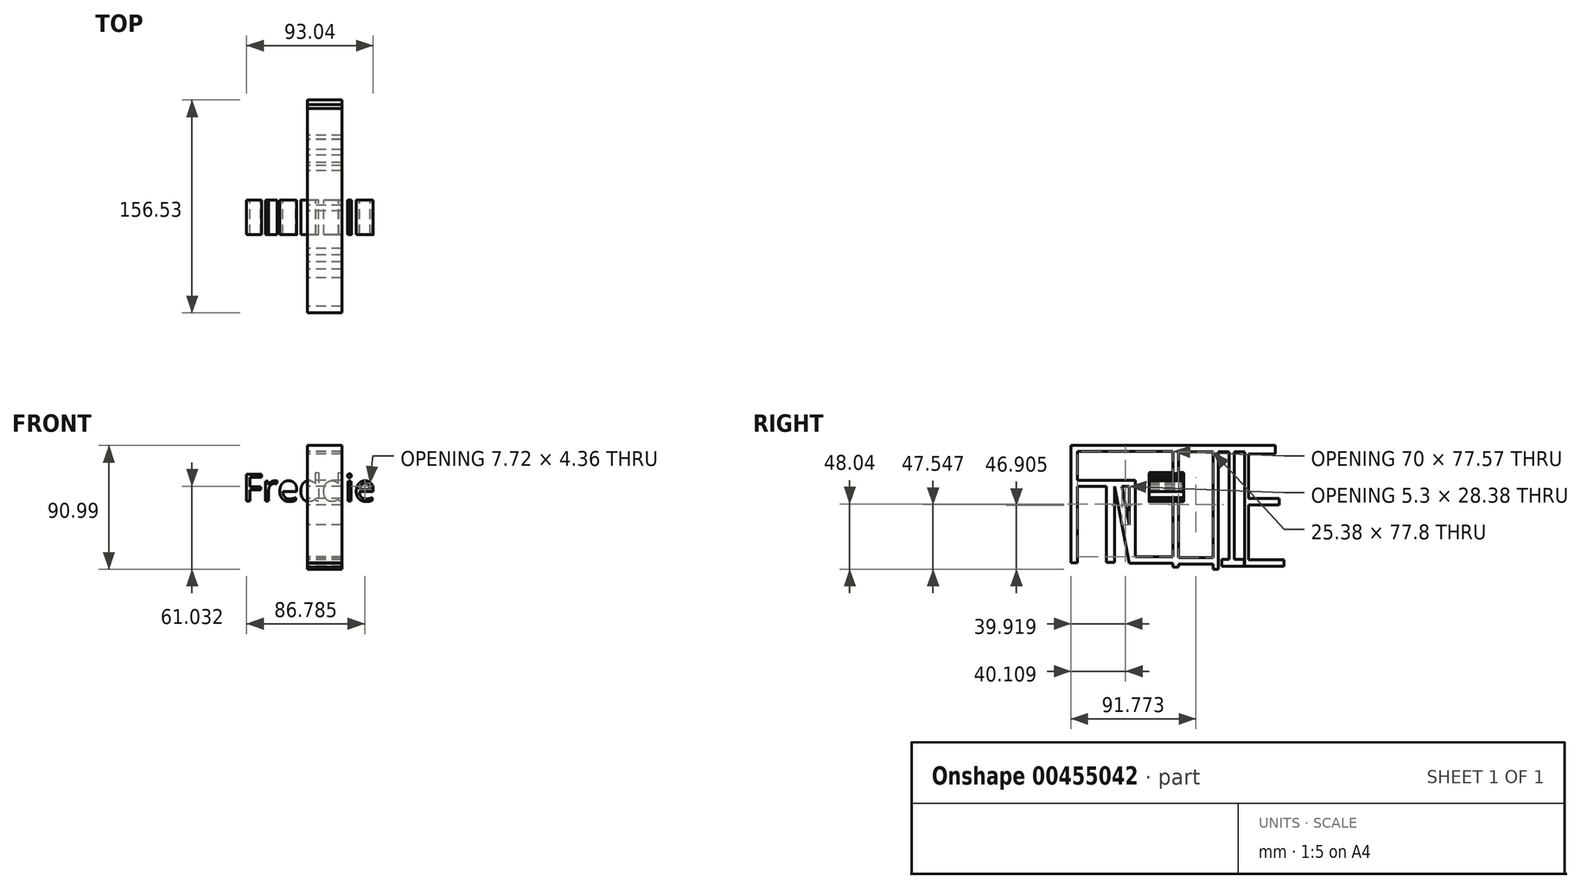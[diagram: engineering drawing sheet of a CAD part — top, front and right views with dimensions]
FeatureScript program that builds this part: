
annotation { "Feature Type Name" : "Feature", "Feature Type Description" : "" }
export const myFeature = defineFeature(function(context is Context, id is Id, definition is map)
    precondition{}
    {
        {
            var Q0;
            Q0=qCreatedBy(makeId("Front.planeOp"),FACE);
            var sketch = newSketch(context, id + "F0", { "sketchPlane" : qUnion([Q0])});
            skText(sketch, "E0", { "text": " Freddie\n", "fontName": "OpenSans-Regular.ttf"});
            const initialGuessF0  = {"E0": [-0.05437, 0, 1, 0, 0.01985]};
            skSetInitialGuess(sketch, initialGuessF0);
            skSolve(sketch);
        }
        {
            var Q0;
            Q0 = qSketchRegion(id + "F0", true);
            var Q1;
            Q1=makeQuery(id+"F0.imprint","IMPRINT",FACE,{"disambiguationData":[TD([[makeQuery(id+"F0.imprint","IMPRINT",EDGE,{"derivedFrom":sQuery(id+"F0.wireOp",EDGE,"E0.sketch_text.stroke-102")}),-1.0]])]});
            var Q2;
            Q2=makeQuery(id+"F0.imprint","IMPRINT",FACE,{"disambiguationData":[TD([[makeQuery(id+"F0.imprint","IMPRINT",EDGE,{"derivedFrom":sQuery(id+"F0.wireOp",EDGE,"E0.sketch_text.stroke-66")}),-1.0]])]});
            var Q3;
            Q3=makeQuery(id+"F0.imprint","IMPRINT",FACE,{"disambiguationData":[TD([[makeQuery(id+"F0.imprint","IMPRINT",EDGE,{"derivedFrom":sQuery(id+"F0.wireOp",EDGE,"E0.sketch_text.stroke-81")}),1.0]])]});
            var Q4;
            Q4=makeQuery(id+"F0.imprint","IMPRINT",FACE,{"disambiguationData":[TD([[makeQuery(id+"F0.imprint","IMPRINT",EDGE,{"derivedFrom":sQuery(id+"F0.wireOp",EDGE,"E0.sketch_text.stroke-57")}),1.0]])]});
            var Q5;
            Q5=makeQuery(id+"F0.imprint","IMPRINT",FACE,{"disambiguationData":[TD([[makeQuery(id+"F0.imprint","IMPRINT",EDGE,{"derivedFrom":sQuery(id+"F0.wireOp",EDGE,"E0.sketch_text.stroke-42")}),-1.0]])]});
            var Q6;
            Q6=makeQuery(id+"F0.imprint","IMPRINT",FACE,{"disambiguationData":[TD([[makeQuery(id+"F0.imprint","IMPRINT",EDGE,{"derivedFrom":sQuery(id+"F0.wireOp",EDGE,"E0.sketch_text.stroke-37")}),1.0]])]});
            var Q7;
            Q7=makeQuery(id+"F0.imprint","IMPRINT",FACE,{"disambiguationData":[TD([[makeQuery(id+"F0.imprint","IMPRINT",EDGE,{"derivedFrom":sQuery(id+"F0.wireOp",EDGE,"E0.sketch_text.stroke-23")}),-1.0]])]});
            var Q8;
            Q8=makeQuery(id+"F0.imprint","IMPRINT",FACE,{"disambiguationData":[TD([[makeQuery(id+"F0.imprint","IMPRINT",EDGE,{"derivedFrom":sQuery(id+"F0.wireOp",EDGE,"E0.sketch_text.stroke-90")}),-1.0]])]});
            var Q9;
            Q9=makeQuery(id+"F0.imprint","IMPRINT",FACE,{"disambiguationData":[TD([[makeQuery(id+"F0.imprint","IMPRINT",EDGE,{"derivedFrom":sQuery(id+"F0.wireOp",EDGE,"E0.sketch_text.stroke-10")}),-1.0]])]});
            var Q10;
            Q10=makeQuery(id+"F0.imprint","IMPRINT",FACE,{"disambiguationData":[TD([[makeQuery(id+"F0.imprint","IMPRINT",EDGE,{"derivedFrom":sQuery(id+"F0.wireOp",EDGE,"E0.sketch_text.stroke-0")}),-1.0]])]});
            extrude(context, id + "F1", {"entities" : qUnion([Q0, Q1, Q2, Q3, Q4, Q5, Q6, Q7, Q8, Q9, Q10]), "depth" : 25.4 * mm});
        }
        {
            var Q0;
            Q0=qCreatedBy(makeId("Right.planeOp"),FACE);
            var sketch = newSketch(context, id + "F2", { "sketchPlane" : qUnion([Q0])});
            skLineSegment(sketch, "E1.bottom", {"start": v(-82.87, 40.93) * mm, "end": v(-77.95, 40.93) * mm});
            skLineSegment(sketch, "E1.top", {"start": v(-82.87, -45.35) * mm, "end": v(-77.95, -45.35) * mm});
            skLineSegment(sketch, "E1.left", {"start": v(-82.87, 40.93) * mm, "end": v(-82.87, -45.35) * mm});
            skLineSegment(sketch, "E1.right", {"start": v(-77.95, 40.93) * mm, "end": v(-77.95, -45.35) * mm});
            skLineSegment(sketch, "E2.bottom", {"start": v(-77.95, 40.93) * mm, "end": v(-35.95, 40.93) * mm});
            skLineSegment(sketch, "E2.top", {"start": v(-77.95, 36.77) * mm, "end": v(-35.95, 36.77) * mm});
            skLineSegment(sketch, "E2.left", {"start": v(-77.95, 40.93) * mm, "end": v(-77.95, 36.77) * mm});
            skLineSegment(sketch, "E2.right", {"start": v(-35.95, 40.93) * mm, "end": v(-35.95, 36.77) * mm});
            skLineSegment(sketch, "E3.bottom", {"start": v(-77.95, 15.2) * mm, "end": v(-35.57, 15.2) * mm});
            skLineSegment(sketch, "E3.top", {"start": v(-77.95, 11.04) * mm, "end": v(-35.57, 11.04) * mm});
            skLineSegment(sketch, "E3.left", {"start": v(-77.95, 15.2) * mm, "end": v(-77.95, 11.04) * mm});
            skLineSegment(sketch, "E3.right", {"start": v(-35.57, 15.2) * mm, "end": v(-35.57, 11.04) * mm});
            skLineSegment(sketch, "E4.bottom", {"start": v(-56.95, 36.77) * mm, "end": v(-50.7, 36.77) * mm});
            skLineSegment(sketch, "E4.top", {"start": v(-56.95, -44.97) * mm, "end": v(-50.7, -44.97) * mm});
            skLineSegment(sketch, "E4.left", {"start": v(-56.95, 36.77) * mm, "end": v(-56.95, -44.97) * mm});
            skLineSegment(sketch, "E4.right", {"start": v(-50.7, 36.77) * mm, "end": v(-50.7, -44.97) * mm});
            skLineSegment(sketch, "E5.bottom", {"start": v(-40.11, 36.77) * mm, "end": v(-35.57, 36.77) * mm});
            skLineSegment(sketch, "E5.top", {"start": v(-40.11, 15.2) * mm, "end": v(-35.57, 15.2) * mm});
            skLineSegment(sketch, "E5.left", {"start": v(-40.11, 36.77) * mm, "end": v(-40.11, 15.2) * mm});
            skLineSegment(sketch, "E5.right", {"start": v(-35.57, 36.77) * mm, "end": v(-35.57, 15.2) * mm});
            skLineSegment(sketch, "E6.bottom", {"start": v(-35.95, 40.93) * mm, "end": v(-7.95, 40.93) * mm});
            skLineSegment(sketch, "E6.top", {"start": v(-35.95, 36.77) * mm, "end": v(-7.95, 36.77) * mm});
            skLineSegment(sketch, "E6.right", {"start": v(-7.95, 40.93) * mm, "end": v(-7.95, 36.77) * mm});
            skLineSegment(sketch, "E7.bottom", {"start": v(-35.57, 11.04) * mm, "end": v(-40.11, 11.04) * mm});
            skLineSegment(sketch, "E7.top", {"start": v(-35.57, -45.72) * mm, "end": v(-40.11, -45.72) * mm});
            skLineSegment(sketch, "E7.left", {"start": v(-35.57, 11.04) * mm, "end": v(-35.57, -45.72) * mm});
            skLineSegment(sketch, "E7.right", {"start": v(-40.11, 11.04) * mm, "end": v(-40.11, -45.72) * mm});
            skLineSegment(sketch, "E8.bottom", {"start": v(-35.57, 15.2) * mm, "end": v(-7.95, 15.2) * mm});
            skLineSegment(sketch, "E8.top", {"start": v(-35.57, 11.04) * mm, "end": v(-7.95, 11.04) * mm});
            skLineSegment(sketch, "E8.right", {"start": v(-7.95, 15.2) * mm, "end": v(-7.95, 11.04) * mm});
            skLineSegment(sketch, "E9.bottom", {"start": v(-35.57, -45.72) * mm, "end": v(-7.95, -45.72) * mm});
            skLineSegment(sketch, "E9.top", {"start": v(-35.57, -40.8) * mm, "end": v(-7.95, -40.8) * mm});
            skLineSegment(sketch, "E9.left", {"start": v(-35.57, -45.72) * mm, "end": v(-35.57, -40.8) * mm});
            skLineSegment(sketch, "E9.right", {"start": v(-7.95, -45.72) * mm, "end": v(-7.95, -40.8) * mm});
            skLineSegment(sketch, "E10.bottom", {"start": v(-7.95, 40.93) * mm, "end": v(-3.79, 40.93) * mm});
            skLineSegment(sketch, "E10.top", {"start": v(-7.95, -48.37) * mm, "end": v(-3.79, -48.37) * mm});
            skLineSegment(sketch, "E10.left", {"start": v(-7.95, 40.93) * mm, "end": v(-7.95, -48.37) * mm});
            skLineSegment(sketch, "E10.right", {"start": v(-3.79, 40.93) * mm, "end": v(-3.79, -48.37) * mm});
            skLineSegment(sketch, "E11", {"start": v(-50.7, 11.04) * mm, "end": v(-40.11, -45.72) * mm});
            skLineSegment(sketch, "E12", {"start": v(-45.41, 11.04) * mm, "end": v(-40.11, -17.34) * mm});
            skPoint(sketch, "E12.startSnap0", {"position": v(-45.41, -17.34) * mm});
            skLineSegment(sketch, "E13", {"start": v(-40.11, -17.34) * mm, "end": v(-40.11, 6.5) * mm});
            skLineSegment(sketch, "E14.bottom", {"start": v(-3.79, 40.93) * mm, "end": v(25.41, 40.93) * mm});
            skLineSegment(sketch, "E14.top", {"start": v(-3.79, 36.39) * mm, "end": v(25.41, 36.39) * mm});
            skLineSegment(sketch, "E14.left", {"start": v(-3.79, 40.93) * mm, "end": v(-3.79, 36.39) * mm});
            skLineSegment(sketch, "E14.right", {"start": v(25.41, 40.93) * mm, "end": v(25.41, 36.39) * mm});
            skLineSegment(sketch, "E15.bottom", {"start": v(21.6, 36.39) * mm, "end": v(25.41, 36.39) * mm});
            skLineSegment(sketch, "E15.top", {"start": v(21.6, -50.06) * mm, "end": v(25.41, -50.06) * mm});
            skLineSegment(sketch, "E15.left", {"start": v(21.6, 36.39) * mm, "end": v(21.6, -50.06) * mm});
            skLineSegment(sketch, "E15.right", {"start": v(25.41, 36.39) * mm, "end": v(25.41, -50.06) * mm});
            skLineSegment(sketch, "E16.bottom", {"start": v(-3.79, -41.41) * mm, "end": v(21.6, -41.41) * mm});
            skLineSegment(sketch, "E16.top", {"start": v(-3.79, -46.24) * mm, "end": v(21.6, -46.24) * mm});
            skLineSegment(sketch, "E16.left", {"start": v(-3.79, -41.41) * mm, "end": v(-3.79, -46.24) * mm});
            skLineSegment(sketch, "E16.right", {"start": v(21.6, -41.41) * mm, "end": v(21.6, -46.24) * mm});
            skLineSegment(sketch, "E17.bottom", {"start": v(25.41, 40.93) * mm, "end": v(44.91, 40.93) * mm});
            skLineSegment(sketch, "E17.top", {"start": v(25.41, 36.39) * mm, "end": v(44.91, 36.39) * mm});
            skLineSegment(sketch, "E17.right", {"start": v(44.91, 40.93) * mm, "end": v(44.91, 36.39) * mm});
            skLineSegment(sketch, "E18.bottom", {"start": v(33.25, 36.39) * mm, "end": v(37.27, 36.39) * mm});
            skLineSegment(sketch, "E18.top", {"start": v(33.25, -47.85) * mm, "end": v(37.27, -47.85) * mm});
            skLineSegment(sketch, "E18.left", {"start": v(33.25, 36.39) * mm, "end": v(33.25, -47.85) * mm});
            skLineSegment(sketch, "E18.right", {"start": v(37.27, 36.39) * mm, "end": v(37.27, -47.85) * mm});
            skPoint(sketch, "E19.oppositeSnap0", {"position": v(35.26, -47.85) * mm});
            skLineSegment(sketch, "E19.bottom", {"start": v(27.82, -42.82) * mm, "end": v(44.5, -42.82) * mm});
            skLineSegment(sketch, "E19.top", {"start": v(27.82, -47.85) * mm, "end": v(44.5, -47.85) * mm});
            skLineSegment(sketch, "E19.left", {"start": v(27.82, -42.82) * mm, "end": v(27.82, -47.85) * mm});
            skLineSegment(sketch, "E19.right", {"start": v(44.5, -42.82) * mm, "end": v(44.5, -47.85) * mm});
            skLineSegment(sketch, "E20.bottom", {"start": v(6.92, 36.39) * mm, "end": v(10.74, 36.39) * mm});
            skLineSegment(sketch, "E20.top", {"start": v(6.92, -41.41) * mm, "end": v(10.74, -41.41) * mm});
            skLineSegment(sketch, "E20.left", {"start": v(6.92, 36.39) * mm, "end": v(6.92, -41.41) * mm});
            skLineSegment(sketch, "E20.right", {"start": v(10.74, 36.39) * mm, "end": v(10.74, -41.41) * mm});
            skLineSegment(sketch, "E21.bottom", {"start": v(44.91, 40.93) * mm, "end": v(67.43, 40.93) * mm});
            skLineSegment(sketch, "E21.top", {"start": v(44.91, 34.58) * mm, "end": v(67.43, 34.58) * mm});
            skLineSegment(sketch, "E21.left", {"start": v(44.91, 40.93) * mm, "end": v(44.91, 34.58) * mm});
            skLineSegment(sketch, "E21.right", {"start": v(67.43, 40.93) * mm, "end": v(67.43, 34.58) * mm});
            skLineSegment(sketch, "E22.bottom", {"start": v(44.91, 34.58) * mm, "end": v(47.73, 34.58) * mm});
            skLineSegment(sketch, "E22.top", {"start": v(44.91, -47.85) * mm, "end": v(47.73, -47.85) * mm});
            skLineSegment(sketch, "E22.left", {"start": v(44.91, 34.58) * mm, "end": v(44.91, -47.85) * mm});
            skLineSegment(sketch, "E22.right", {"start": v(47.73, 34.58) * mm, "end": v(47.73, -47.85) * mm});
            skLineSegment(sketch, "E23.bottom", {"start": v(47.73, -47.85) * mm, "end": v(73.66, -47.85) * mm});
            skLineSegment(sketch, "E23.top", {"start": v(47.73, -43.02) * mm, "end": v(73.66, -43.02) * mm});
            skLineSegment(sketch, "E23.left", {"start": v(47.73, -47.85) * mm, "end": v(47.73, -43.02) * mm});
            skLineSegment(sketch, "E23.right", {"start": v(73.66, -47.85) * mm, "end": v(73.66, -43.02) * mm});
            skLineSegment(sketch, "E24.bottom", {"start": v(47.73, 2.01) * mm, "end": v(70.24, 2.01) * mm});
            skLineSegment(sketch, "E24.top", {"start": v(47.73, -2.81) * mm, "end": v(70.24, -2.81) * mm});
            skLineSegment(sketch, "E24.left", {"start": v(47.73, 2.01) * mm, "end": v(47.73, -2.81) * mm});
            skLineSegment(sketch, "E24.right", {"start": v(70.24, 2.01) * mm, "end": v(70.24, -2.81) * mm});
            skSolve(sketch);
        }
        {
            var Q0;
            Q0 = qSketchRegion(id + "F2", true);
            extrude(context, id + "F3", {"entities" : qUnion([Q0]), "depth" : 25.4 * mm});
        }
    });
